# Revit family: 63_UN_WallMount_SWF MINI_Norton
name_source: partatom
category: Lighting Fixtures
units: mm (PartAtom-declared; Revit-internal decimal feet)

## family parameters
Always vertical = Yes
Cut with Voids When Loaded = Yes
Light Source = Yes
OmniClass Number = 23.80.70.11.14.11
OmniClass Title = Downlights
Part Type = Normal
Room Calculation Point = Yes
Round Connector Dimension = Use Diameter
Shared = No
Work Plane-Based = No

## types (4) — shared parameters
Assembly Code = 63.0
Calc_Symbol_Length = 160 mm  [stored 0.524934 ft]
Calc_Symbol_Width = 155 mm  [stored 0.50853 ft]
Color Filter = 16777215
Description = IP66 / IK10
Dimming Lamp Color Temperature Shift = <None>
Emit Shape Visible in Rendering = No
Emit from Rectangle Length = 57 mm  [stored 0.187008 ft]
Emit from Rectangle Width = 93 mm  [stored 0.305118 ft]
Housing_Material = Anthracite
IfcExportAs = IfcLightFixtureType
IfcExportType = USERDEFINED
Lamp = LED
Manufacturer = Norton
Model = SWF
Tilt Angle = 90.00°
URL = https://www.norton.nl
Voltage = 230 V
Weight = 1.9kg

## per-type parameters (varying)
| type | Apparent Load | Luminous Flux (lm) | Photometric Web File | Wattage Comments |
| SWFMINI83LM2500 | 20 VA | 2500 lm | SWFMINI83LM2500_LDT.ies | 20W |
| SWFMINI83LM1200 | 10 VA | 1250 lm | SWFMINI83LM1200_LDT.ies | 10W |
| SWFMINI84LM1200 | 10 VA | 1250 lm | SWFMINI84LM1200_LDT.ies | 10W |
| SWFMINI84LM2500 | 20 VA | 2500 lm | SWFMINI84LM2500_LDT.ies | 20W |

note: [stored X ft] marks values corroborated as IEEE doubles in the binary element streams (Revit-internal decimal feet)

## geometry (parser evidence)
native form markers: Sweep x6
no freeform markers — native parametric forms only
